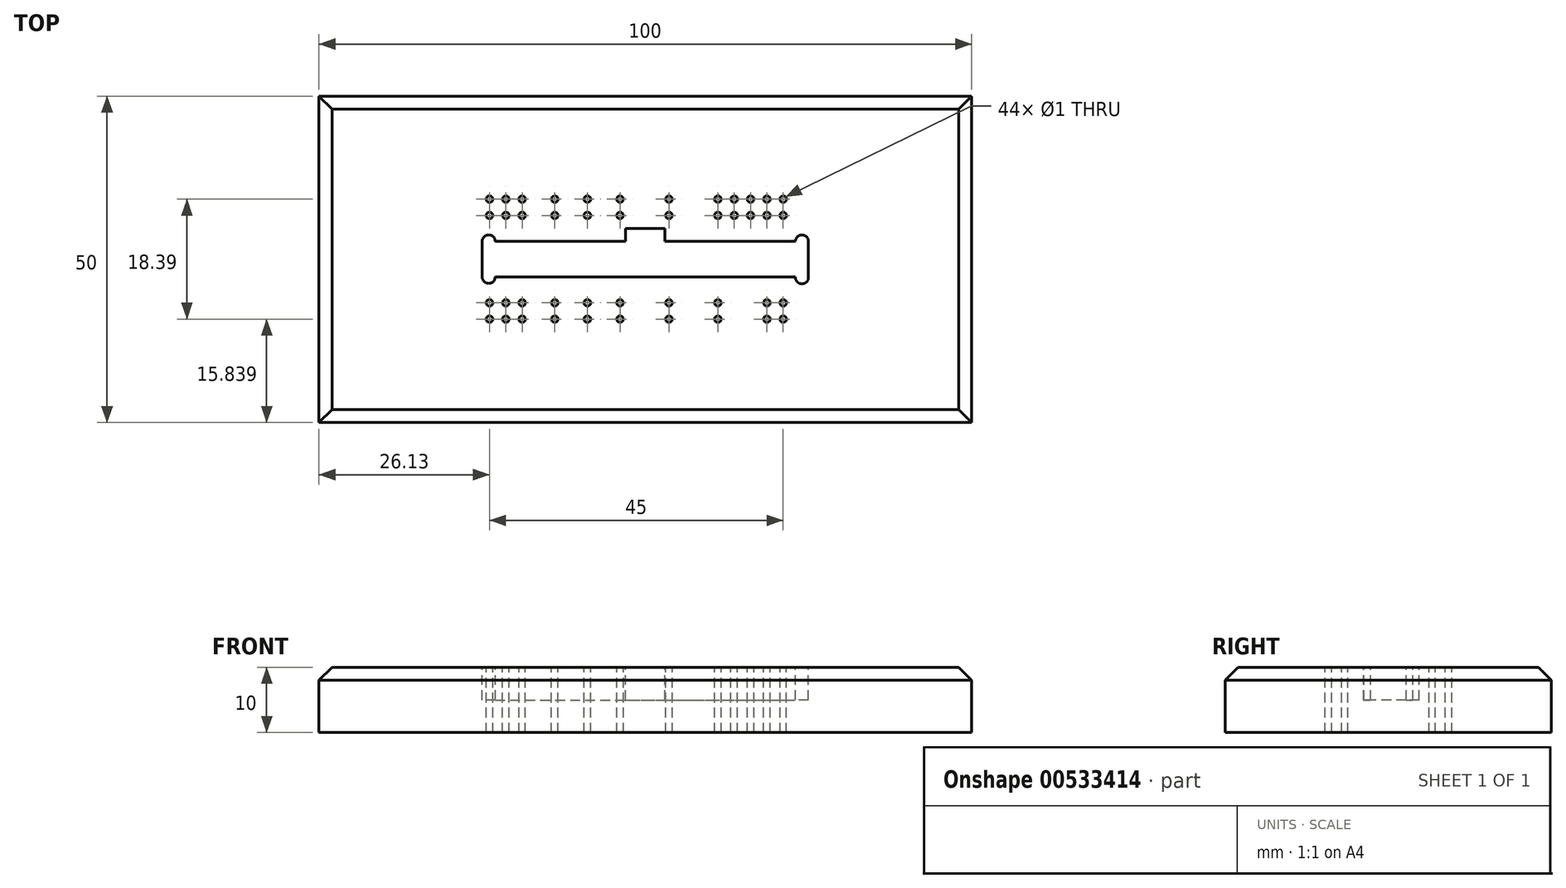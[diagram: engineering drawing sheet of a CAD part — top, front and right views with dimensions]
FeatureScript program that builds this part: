
annotation { "Feature Type Name" : "Feature", "Feature Type Description" : "" }
export const myFeature = defineFeature(function(context is Context, id is Id, definition is map)
    precondition{}
    {
        {
            var Q0;
            Q0=qCreatedBy(makeId("Top.planeOp"),FACE);
            var sketch = newSketch(context, id + "F0", { "sketchPlane" : qUnion([Q0])});
            skLineSegment(sketch, "E0.bottom", {"start": v(0, 0) * mm, "end": v(100, 0) * mm});
            skLineSegment(sketch, "E0.top", {"start": v(0, 50) * mm, "end": v(100, 50) * mm});
            skLineSegment(sketch, "E0.left", {"start": v(0, 0) * mm, "end": v(0, 50) * mm});
            skLineSegment(sketch, "E0.right", {"start": v(100, 0) * mm, "end": v(100, 50) * mm});
            skSolve(sketch);
        }
        {
            var Q0;
            Q0=makeQuery(id+"F0.imprint","IMPRINT",FACE,{"disambiguationData":[TD([[makeQuery(id+"F0.imprint","IMPRINT",EDGE,{"derivedFrom":sQuery(id+"F0.wireOp",EDGE,"E0.bottom")}),1.0]])]});
            extrude(context, id + "F1", {"entities" : qUnion([Q0]), "depth" : 10 * mm, "offsetDistance" : 25 * mm});
        }
        {
            var Q0;
            Q0=makeQuery(id+"F1.opExtrude","CAP_FACE",FACE,{"disambiguationData":[OSD([sQuery(id+"F0.wireOp",EDGE,"E0.bottom"),sQuery(id+"F0.wireOp",EDGE,"E0.top"),sQuery(id+"F0.wireOp",EDGE,"E0.left"),sQuery(id+"F0.wireOp",EDGE,"E0.right")])],"isStart":false});
            var sketch = newSketch(context, id + "F2", { "sketchPlane" : qUnion([Q0])});
            skLineSegment(sketch, "E1.top", {"start": v(27, 22.32) * mm, "end": v(73, 22.32) * mm});
            skLineSegment(sketch, "E1.left", {"start": v(25, 27.75) * mm, "end": v(25, 22.32) * mm});
            skLineSegment(sketch, "E1.right", {"start": v(75, 27.75) * mm, "end": v(75, 22.25) * mm});
            skLineSegment(sketch, "E2", {"start": v(47, 27.75) * mm, "end": v(47, 29.75) * mm});
            skLineSegment(sketch, "E3", {"start": v(47, 29.75) * mm, "end": v(53, 29.75) * mm});
            skLineSegment(sketch, "E4.trimOffspring", {"start": v(53, 27.75) * mm, "end": v(73, 27.75) * mm});
            skLineSegment(sketch, "E5", {"start": v(50, 0) * mm, "end": v(50, 60.92) * mm, "construction": true});
            skLineSegment(sketch, "E6", {"start": v(53, 29.75) * mm, "end": v(53, 27.75) * mm});
            skArc(sketch, "E7", {"start": v(27, 27.75) * mm, "mid": v(26, 28.75) * mm, "end": v(25, 27.75) * mm});
            skArc(sketch, "E8", {"start": v(25, 22.32) * mm, "mid": v(26, 21.32) * mm, "end": v(27, 22.32) * mm});
            skArc(sketch, "E9", {"start": v(73, 22.32) * mm, "mid": v(73.97, 21.25) * mm, "end": v(75, 22.25) * mm});
            skArc(sketch, "E10", {"start": v(75, 27.75) * mm, "mid": v(74, 28.75) * mm, "end": v(73, 27.75) * mm});
            skLineSegment(sketch, "E11.trimOffspring", {"start": v(27, 27.75) * mm, "end": v(47, 27.75) * mm});
            skSolve(sketch);
        }
        {
            var Q0;
            Q0=makeQuery(id+"F2.imprint","IMPRINT",FACE,{"disambiguationData":[TD([[makeQuery(id+"F2.imprint","IMPRINT",EDGE,{"derivedFrom":sQuery(id+"F2.wireOp",EDGE,"E1.bottom")}),-1.0]])]});
            var Q1;
            Q1=makeQuery(id+"F2.imprint","IMPRINT",FACE,{"disambiguationData":[TD([[makeQuery(id+"F2.imprint","IMPRINT",EDGE,{"derivedFrom":sQuery(id+"F2.wireOp",EDGE,"E1.top")}),1.0]])]});
            extrude(context, id + "F3", {"entities" : qUnion([Q0, Q1]), "operationType" : NewBodyOperationType.REMOVE, "oppositeDirection" : true, "depth" : 5 * mm, "offsetDistance" : 25 * mm});
        }
        {
            var Q0;
            Q0=makeQuery(id+"F1.opExtrude","CAP_FACE",FACE,{"disambiguationData":[OSD([sQuery(id+"F0.wireOp",EDGE,"E0.bottom"),sQuery(id+"F0.wireOp",EDGE,"E0.top"),sQuery(id+"F0.wireOp",EDGE,"E0.left"),sQuery(id+"F0.wireOp",EDGE,"E0.right")])],"isStart":false});
            var sketch = newSketch(context, id + "F4", { "sketchPlane" : qUnion([Q0])});
            skCircle(sketch, "E12", {"center": v(26.13, 31.73) * mm, "radius": 0.5 * mm});
            skCircle(sketch, "E13.1.0.0", {"center": v(28.63, 31.73) * mm, "radius": 0.5 * mm});
            skCircle(sketch, "E13.2.0.0", {"center": v(31.13, 31.73) * mm, "radius": 0.5 * mm});
            skCircle(sketch, "E13.4.0.0", {"center": v(36.13, 31.73) * mm, "radius": 0.5 * mm});
            skCircle(sketch, "E13.6.0.0", {"center": v(41.13, 31.73) * mm, "radius": 0.5 * mm});
            skCircle(sketch, "E13.8.0.0", {"center": v(46.13, 31.73) * mm, "radius": 0.5 * mm});
            skCircle(sketch, "E13.11.0.0", {"center": v(53.63, 31.73) * mm, "radius": 0.5 * mm});
            skCircle(sketch, "E13.14.0.0", {"center": v(61.13, 31.73) * mm, "radius": 0.5 * mm});
            skCircle(sketch, "E13.15.0.0", {"center": v(63.63, 31.73) * mm, "radius": 0.5 * mm});
            skCircle(sketch, "E13.16.0.0", {"center": v(66.13, 31.73) * mm, "radius": 0.5 * mm});
            skCircle(sketch, "E13.17.0.0", {"center": v(68.63, 31.73) * mm, "radius": 0.5 * mm});
            skCircle(sketch, "E13.18.0.0", {"center": v(71.13, 31.73) * mm, "radius": 0.5 * mm});
            skLineSegment(sketch, "E13.direction1", {"start": v(26.13, 31.73) * mm, "end": v(28.63, 31.73) * mm, "construction": true});
            skLineSegment(sketch, "E14", {"start": v(18.51, 25.03) * mm, "end": v(81.98, 25.03) * mm, "construction": true});
            skPoint(sketch, "E14.startSnap0", {"position": v(25, 25.03) * mm});
            skLineSegment(sketch, "E15.MirrorCS", {"start": v(26.13, 18.34) * mm, "end": v(28.63, 18.34) * mm, "construction": true});
            skCircle(sketch, "E16.MirrorC", {"center": v(71.13, 18.34) * mm, "radius": 0.5 * mm});
            skCircle(sketch, "E17.MirrorC", {"center": v(61.13, 18.34) * mm, "radius": 0.5 * mm});
            skCircle(sketch, "E18.MirrorC", {"center": v(26.13, 18.34) * mm, "radius": 0.5 * mm});
            skCircle(sketch, "E19.MirrorC", {"center": v(28.63, 18.34) * mm, "radius": 0.5 * mm});
            skCircle(sketch, "E20.MirrorC", {"center": v(31.13, 18.34) * mm, "radius": 0.5 * mm});
            skCircle(sketch, "E21.MirrorC", {"center": v(36.13, 18.34) * mm, "radius": 0.5 * mm});
            skCircle(sketch, "E22.MirrorC", {"center": v(41.13, 18.34) * mm, "radius": 0.5 * mm});
            skCircle(sketch, "E23.MirrorC", {"center": v(46.13, 18.34) * mm, "radius": 0.5 * mm});
            skCircle(sketch, "E24.MirrorC", {"center": v(53.63, 18.34) * mm, "radius": 0.5 * mm});
            skCircle(sketch, "E25.MirrorC", {"center": v(68.63, 18.34) * mm, "radius": 0.5 * mm});
            skCircle(sketch, "E26", {"center": v(26.13, 34.23) * mm, "radius": 0.5 * mm});
            skCircle(sketch, "E27.1.0.0", {"center": v(28.63, 34.23) * mm, "radius": 0.5 * mm});
            skCircle(sketch, "E27.2.0.0", {"center": v(31.13, 34.23) * mm, "radius": 0.5 * mm});
            skCircle(sketch, "E27.4.0.0", {"center": v(36.13, 34.23) * mm, "radius": 0.5 * mm});
            skCircle(sketch, "E27.6.0.0", {"center": v(41.13, 34.23) * mm, "radius": 0.5 * mm});
            skCircle(sketch, "E27.8.0.0", {"center": v(46.13, 34.23) * mm, "radius": 0.5 * mm});
            skCircle(sketch, "E27.11.0.0", {"center": v(53.63, 34.23) * mm, "radius": 0.5 * mm});
            skCircle(sketch, "E27.14.0.0", {"center": v(61.13, 34.23) * mm, "radius": 0.5 * mm});
            skCircle(sketch, "E27.15.0.0", {"center": v(63.63, 34.23) * mm, "radius": 0.5 * mm});
            skCircle(sketch, "E27.16.0.0", {"center": v(66.13, 34.23) * mm, "radius": 0.5 * mm});
            skCircle(sketch, "E27.17.0.0", {"center": v(68.63, 34.23) * mm, "radius": 0.5 * mm});
            skCircle(sketch, "E27.18.0.0", {"center": v(71.13, 34.23) * mm, "radius": 0.5 * mm});
            skLineSegment(sketch, "E27.direction1", {"start": v(26.13, 34.23) * mm, "end": v(28.63, 34.23) * mm, "construction": true});
            skCircle(sketch, "E28.MirrorC", {"center": v(41.13, 15.84) * mm, "radius": 0.5 * mm});
            skLineSegment(sketch, "E29.MirrorCS", {"start": v(26.13, 15.84) * mm, "end": v(28.63, 15.84) * mm, "construction": true});
            skCircle(sketch, "E30.MirrorC", {"center": v(61.13, 15.84) * mm, "radius": 0.5 * mm});
            skCircle(sketch, "E31.MirrorC", {"center": v(36.13, 15.84) * mm, "radius": 0.5 * mm});
            skCircle(sketch, "E32.MirrorC", {"center": v(53.63, 15.84) * mm, "radius": 0.5 * mm});
            skCircle(sketch, "E33.MirrorC", {"center": v(46.13, 15.84) * mm, "radius": 0.5 * mm});
            skCircle(sketch, "E34.MirrorC", {"center": v(71.13, 15.84) * mm, "radius": 0.5 * mm});
            skCircle(sketch, "E35.MirrorC", {"center": v(31.13, 15.84) * mm, "radius": 0.5 * mm});
            skCircle(sketch, "E36.MirrorC", {"center": v(26.13, 15.84) * mm, "radius": 0.5 * mm});
            skCircle(sketch, "E37.MirrorC", {"center": v(68.63, 15.84) * mm, "radius": 0.5 * mm});
            skCircle(sketch, "E38.MirrorC", {"center": v(28.63, 15.84) * mm, "radius": 0.5 * mm});
            skSolve(sketch);
        }
        {
            var Q0;
            Q0 = qSketchRegion(id + "F4", true);
            extrude(context, id + "F5", {"entities" : qUnion([Q0]), "operationType" : NewBodyOperationType.REMOVE, "endBound" : BoundingType.THROUGH_ALL, "oppositeDirection" : true, "depth" : 5 * mm, "offsetDistance" : 25 * mm});
        }
        {
            var Q0;
            Q0=makeQuery(id+"F1.opExtrude","CAP_EDGE",EDGE,{"disambiguationData":[OSD([sQuery(id+"F0.wireOp",EDGE,"E0.bottom")])],"isStart":false});
            var Q1;
            Q1=makeQuery(id+"F1.opExtrude","CAP_EDGE",EDGE,{"disambiguationData":[OSD([sQuery(id+"F0.wireOp",EDGE,"E0.left")])],"isStart":false});
            var Q2;
            Q2=makeQuery(id+"F1.opExtrude","CAP_EDGE",EDGE,{"disambiguationData":[OSD([sQuery(id+"F0.wireOp",EDGE,"E0.top")])],"isStart":false});
            var Q3;
            Q3=makeQuery(id+"F1.opExtrude","CAP_EDGE",EDGE,{"disambiguationData":[OSD([sQuery(id+"F0.wireOp",EDGE,"E0.right")])],"isStart":false});
            chamfer(context, id + "F6", {"entities" : qUnion([Q0, Q1, Q2, Q3]), "width" : 2 * mm, "tangentPropagation" : true});
        }
    });
